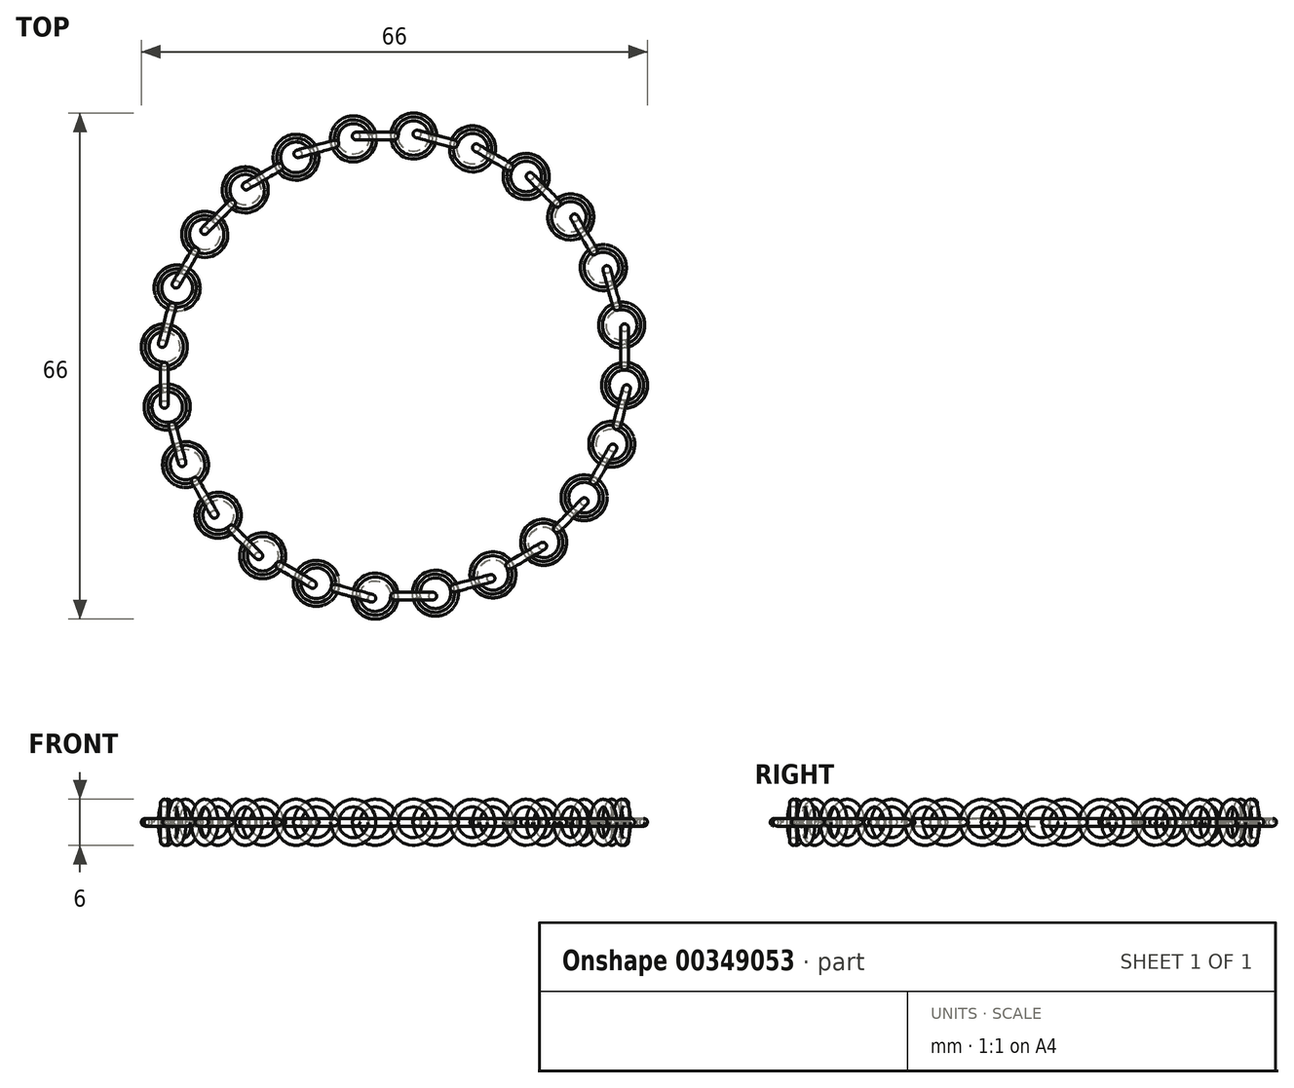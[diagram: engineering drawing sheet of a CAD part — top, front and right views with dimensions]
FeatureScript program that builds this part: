
annotation { "Feature Type Name" : "Feature", "Feature Type Description" : "" }
export const myFeature = defineFeature(function(context is Context, id is Id, definition is map)
    precondition{}
    {
        {
            var Q0;
            Q0=qCreatedBy(makeId("Top.planeOp"),FACE);
            var sketch = newSketch(context, id + "F0", { "sketchPlane" : qUnion([Q0])});
            skCircle(sketch, "E0", {"center": v(-2.5, -30) * mm, "radius": 2.5 * mm});
            skSolve(sketch);
        }
        {
            var Q0;
            Q0=qCreatedBy(makeId("Front.planeOp"),FACE);
            var Q1;
            Q1=sQuery(id+"F0.wireOp",VERTEX,"E0.center");
            cPlane(context, id + "F1", {"entities" : qUnion([Q0, Q1]), "cplaneType" : CPlaneType.PLANE_POINT, "offset" : 25 * mm, "width" : 150 * mm, "height" : 150 * mm});
        }
        {
            var Q0;
            Q0=qCreatedBy(id+"F1.planeOp",FACE);
            var sketch = newSketch(context, id + "F2", { "sketchPlane" : qUnion([Q0])});
            skCircle(sketch, "E1", {"center": v(0, 0) * mm, "radius": 0.5 * mm});
            skSolve(sketch);
        }
        {
            var Q0;
            Q0=makeQuery(id+"F2.imprint","IMPRINT",FACE,{"disambiguationData":[TD([[makeQuery(id+"F2.imprint","IMPRINT",EDGE,{"derivedFrom":sQuery(id+"F2.wireOp",EDGE,"E1")}),1.0]])]});
            var Q1;
            Q1=sQuery(id+"F0.wireOp",EDGE,"E0");
            sweep(context, id + "F3", {"profiles" : qUnion([Q0]), "path" : qUnion([Q1])});
        }
        {
            var Q0;
            Q0=qCreatedBy(id+"F1.planeOp",FACE);
            var sketch = newSketch(context, id + "F4", { "sketchPlane" : qUnion([Q0])});
            skCircle(sketch, "E2", {"center": v(2.5, 0) * mm, "radius": 2.5 * mm});
            skSolve(sketch);
        }
        {
            var Q0;
            Q0=qCreatedBy(makeId("Top.planeOp"),FACE);
            var sketch = newSketch(context, id + "F5", { "sketchPlane" : qUnion([Q0])});
            skCircle(sketch, "E3", {"center": v(0, -30) * mm, "radius": 0.5 * mm});
            skSolve(sketch);
        }
        {
            var Q0;
            Q0 = qSketchRegion(id + "F5", true);
            var Q1;
            Q1 = qConstructionFilter(qBodyType(qCreatedBy(id + "F4" ,EDGE), BodyType.WIRE), ConstructionObject.NO);
            sweep(context, id + "F6", {"operationType" : NewBodyOperationType.ADD, "profiles" : qUnion([Q0]), "path" : qUnion([Q1])});
        }
        {
            var Q0;
            Q0=qCreatedBy(makeId("Front.planeOp"),FACE);
            var sketch = newSketch(context, id + "F7", { "sketchPlane" : qUnion([Q0])});
            skLineSegment(sketch, "E4", {"start": v(0, -18.83) * mm, "end": v(0, 21.06) * mm, "construction": true});
            skSolve(sketch);
        }
        {
            var Q0;
            Q0=makeQuery(id+"F3.opSweep","SWEPT_BODY",BODY,{"disambiguationData":[OSD([sQuery(id+"F0.wireOp",EDGE,"E0"),sQuery(id+"F2.wireOp",EDGE,"E1")])]});
            var Q1;
            Q1=sQuery(id+"F7.wireOp",EDGE,"E4");
            circularPattern(context, id + "F8", {"entities" : qUnion([Q0]), "axis" : qUnion([Q1]), "angle" : 360 * degree, "instanceCount" : 24, "equalSpace" : true});
        }
    });
